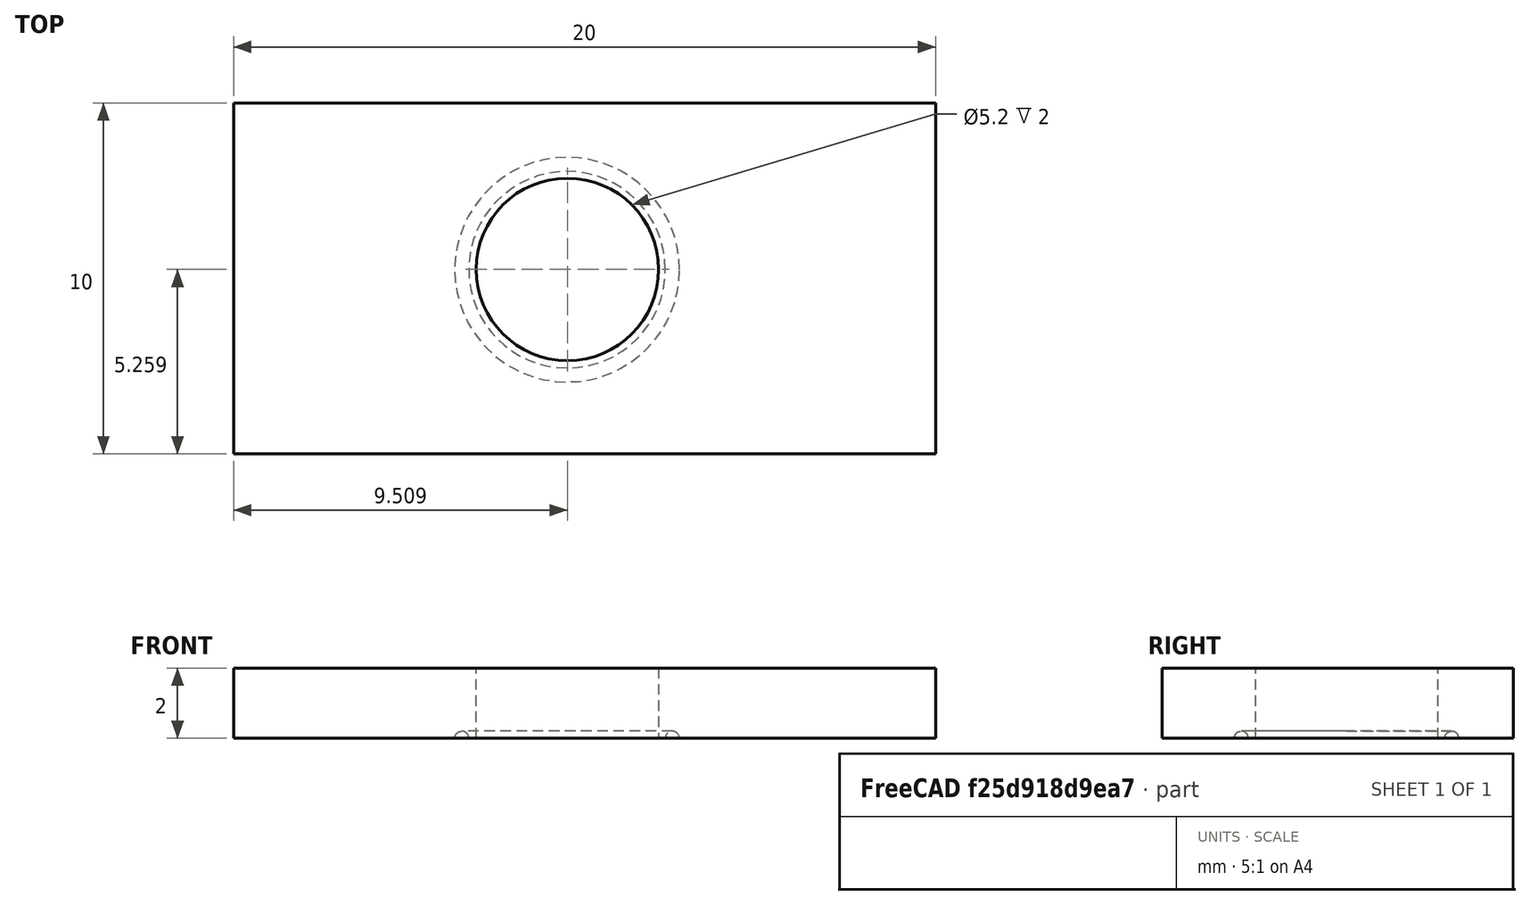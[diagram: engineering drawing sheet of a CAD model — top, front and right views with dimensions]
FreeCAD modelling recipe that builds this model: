
FCSTD DOCUMENT  (FreeCAD 0.16R6712 (Git))
Label: PLAQUE SUP
License: All rights reserved
LicenseURL: http://en.wikipedia.org/wiki/All_rights_reserved
objects: Part::Box×1, Sketcher::SketchObject×1, PartDesign::Pocket×1, Part::Torus×1, Part::Cut×1, Mesh::Feature×1
note: 6 computed .brp shape members not serialized (recipe doc carries the construction recipe); baked Part::Feature solids carry a one-line shape summary decoded from their .brp

FEATURE [Part::Box] Box  label="Cube"
  Height = 2
  Length = 20
  Width = 10
FEATURE [Sketcher::SketchObject] Sketch
  Placement = pos=(0,0,2) rot=(0,0,1;0rad)
  Support = -> Box [Face6]
  sketch-geometry (1):
    g0: Circle CenterX=9.50947 CenterY=5.25875 CenterZ=0 NormalX=0 NormalY=0 NormalZ=1 Radius=2.6
  constraints (1):
    c: Radius(g0) = 2.6
FEATURE [PartDesign::Pocket] Pocket
  Length = 5
  Sketch = -> Sketch
  Type = 0
FEATURE [Part::Torus] Torus  label="Tore"
  Angle1 = -180
  Angle2 = 180
  Angle3 = 360
  Placement = pos=(9.5,5.25,0) rot=(0,0,1;0rad)
  Radius1 = 3
  Radius2 = 0.2
FEATURE [Part::Cut] Cut
  Base = -> Pocket
  Tool = -> Torus
FEATURE [Mesh::Feature] Mesh  label="Cut (Meshed)"
